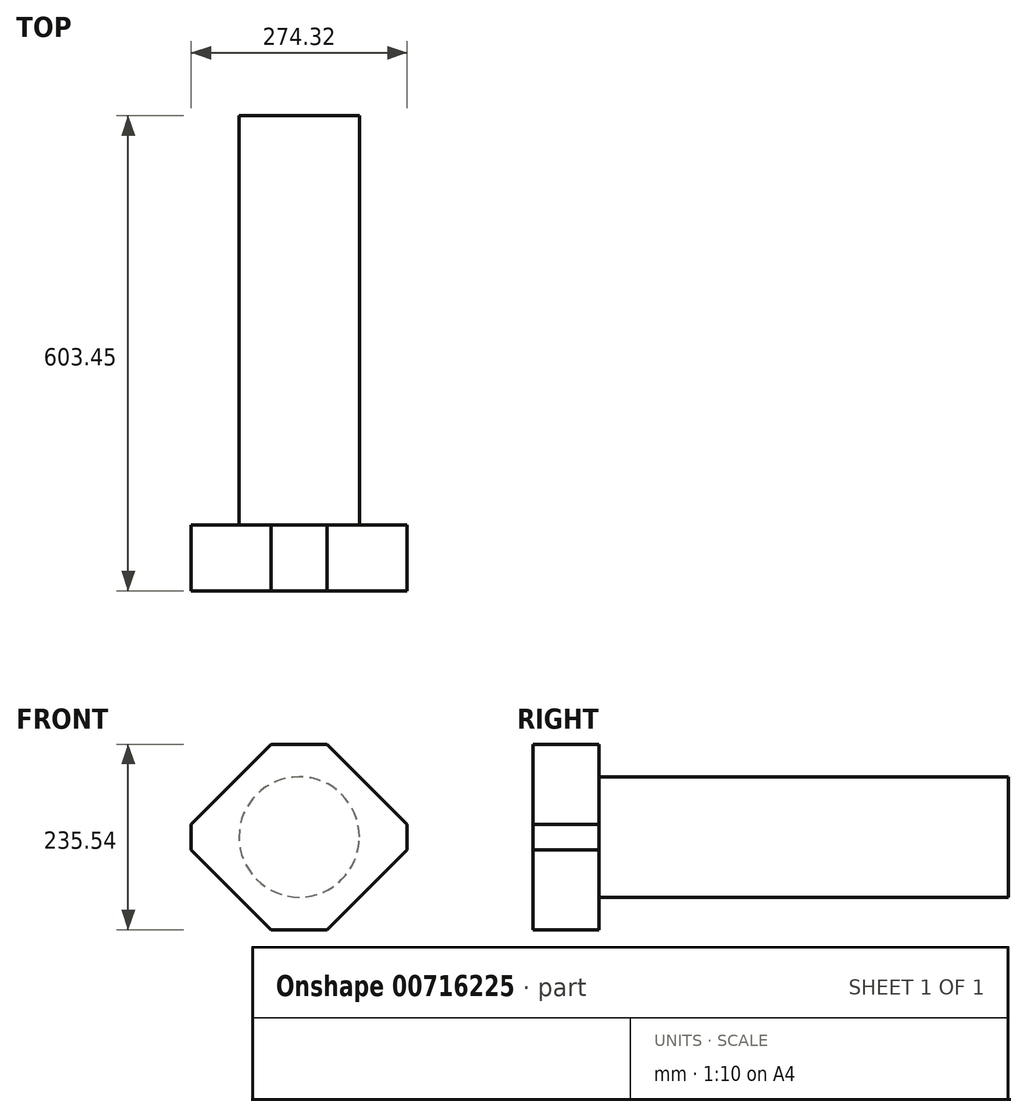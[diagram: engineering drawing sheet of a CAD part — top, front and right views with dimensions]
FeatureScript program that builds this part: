
annotation { "Feature Type Name" : "Feature", "Feature Type Description" : "" }
export const myFeature = defineFeature(function(context is Context, id is Id, definition is map)
    precondition{}
    {
        {
            var Q0;
            Q0=qCreatedBy(makeId("Front.planeOp"),FACE);
            var sketch = newSketch(context, id + "F0", { "sketchPlane" : qUnion([Q0])});
            skCircle(sketch, "E0", {"center": v(0, 0) * mm, "radius": 76.39 * mm});
            skSolve(sketch);
        }
        {
            var Q0;
            Q0=makeQuery(id+"F0.imprint","IMPRINT",FACE,{"disambiguationData":[TD([[makeQuery(id+"F0.imprint","IMPRINT",EDGE,{"derivedFrom":sQuery(id+"F0.wireOp",EDGE,"E0")}),1.0]])]});
            extrude(context, id + "F1", {"entities" : qUnion([Q0]), "oppositeDirection" : true, "depth" : 519.67 * mm, "offsetDistance" : 25.4 * mm});
        }
        {
            var Q0;
            Q0=qCreatedBy(makeId("Front.planeOp"),FACE);
            var sketch = newSketch(context, id + "F2", { "sketchPlane" : qUnion([Q0])});
            skLineSegment(sketch, "E1.bottom", {"start": v(137.16, 117.77) * mm, "end": v(-137.16, 117.77) * mm});
            skLineSegment(sketch, "E1.top", {"start": v(137.16, -117.77) * mm, "end": v(-137.16, -117.77) * mm});
            skLineSegment(sketch, "E1.left", {"start": v(137.16, 117.77) * mm, "end": v(137.16, -117.77) * mm});
            skLineSegment(sketch, "E1.right", {"start": v(-137.16, 117.77) * mm, "end": v(-137.16, -117.77) * mm});
            skPoint(sketch, "E1.middle", {"position": v(0, 0) * mm});
            skSolve(sketch);
        }
        {
            var Q0;
            Q0 = qSketchRegion(id + "F2", true);
            extrude(context, id + "F3", {"entities" : qUnion([Q0]), "operationType" : NewBodyOperationType.ADD, "depth" : 83.78 * mm, "offsetDistance" : 25.4 * mm});
        }
        {
            var Q0;
            Q0=makeQuery(id+"F3.opExtrude","SWEPT_EDGE",EDGE,{"disambiguationData":[OSD([sQuery(id+"F2.wireOp",EDGE,"E1.bottom"),sQuery(id+"F2.wireOp",EDGE,"E1.left")])]});
            var Q1;
            Q1=makeQuery(id+"F3.opExtrude","SWEPT_EDGE",EDGE,{"disambiguationData":[OSD([sQuery(id+"F2.wireOp",EDGE,"E1.bottom"),sQuery(id+"F2.wireOp",EDGE,"E1.right")])]});
            var Q2;
            Q2=makeQuery(id+"F3.opExtrude","SWEPT_EDGE",EDGE,{"disambiguationData":[OSD([sQuery(id+"F2.wireOp",EDGE,"E1.top"),sQuery(id+"F2.wireOp",EDGE,"E1.right")])]});
            var Q3;
            Q3=makeQuery(id+"F3.opExtrude","SWEPT_EDGE",EDGE,{"disambiguationData":[OSD([sQuery(id+"F2.wireOp",EDGE,"E1.top"),sQuery(id+"F2.wireOp",EDGE,"E1.left")])]});
            chamfer(context, id + "F4", {"entities" : qUnion([Q0, Q1, Q2, Q3]), "width" : 101.6 * mm, "tangentPropagation" : true});
        }
    });
